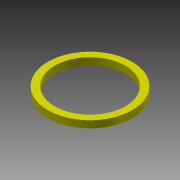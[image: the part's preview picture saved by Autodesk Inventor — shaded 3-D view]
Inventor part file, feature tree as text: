
AUTODESK INVENTOR PART (.ipt)
format: ipt  version: 2013 (Build 170138000, 138)  size: 75,264 bytes
history: native  units: mm
features: extrude x1, sketch x1
ambient origin geometry x8: Origin, YZ Plane, XZ Plane, XY Plane, X Axis, Y Axis, Z Axis, Center Point
bodies: Solid1 (feature_tree)
feature tree (2):
  extrude  "Extrusion1"  Depth=18.0mm
  sketch  "Sketch1"  dims[d0=15.1mm d2=18.0mm d3=1.5mm d4=0.0mm]
